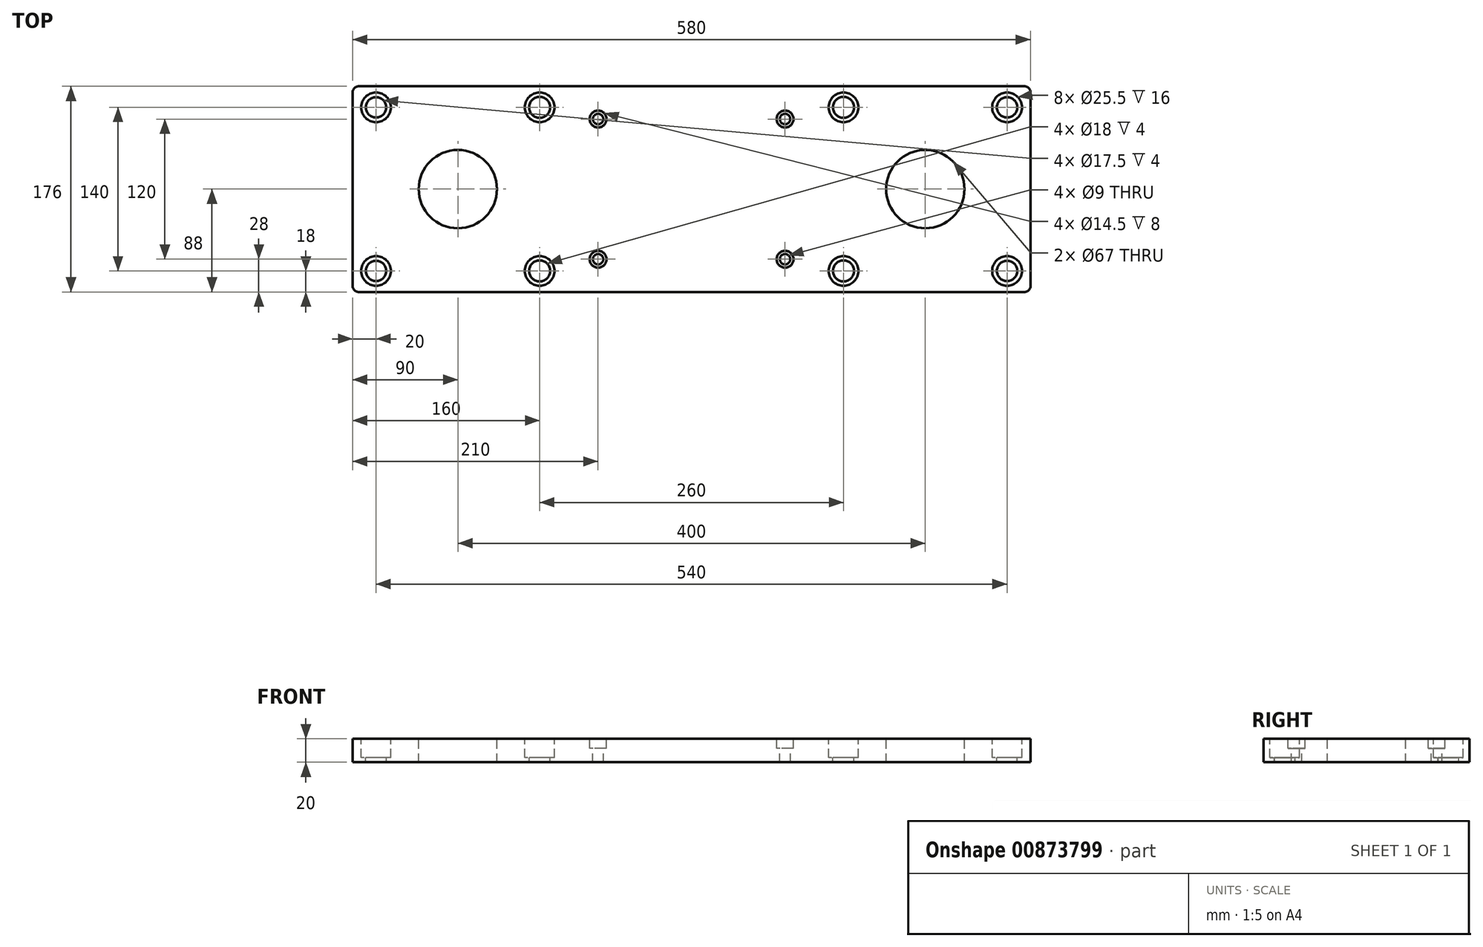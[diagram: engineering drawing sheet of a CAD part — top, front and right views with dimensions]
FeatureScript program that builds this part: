
annotation { "Feature Type Name" : "Feature", "Feature Type Description" : "" }
export const myFeature = defineFeature(function(context is Context, id is Id, definition is map)
    precondition{}
    {
        {
            var Q0;
            Q0=qCreatedBy(makeId("Top.planeOp"),FACE);
            var sketch = newSketch(context, id + "F0", { "sketchPlane" : qUnion([Q0])});
            skLineSegment(sketch, "E0.bottom", {"start": v(290, -88) * mm, "end": v(-290, -88) * mm});
            skLineSegment(sketch, "E0.top", {"start": v(290, 88) * mm, "end": v(-290, 88) * mm});
            skLineSegment(sketch, "E0.left", {"start": v(290, -88) * mm, "end": v(290, 88) * mm});
            skLineSegment(sketch, "E0.right", {"start": v(-290, -88) * mm, "end": v(-290, 88) * mm});
            skPoint(sketch, "E0.middle", {"position": v(0, 0) * mm});
            skLineSegment(sketch, "E1.bottom", {"start": v(-270, -70) * mm, "end": v(-130, -70) * mm});
            skLineSegment(sketch, "E1.top", {"start": v(-270, 70) * mm, "end": v(-130, 70) * mm});
            skLineSegment(sketch, "E1.left", {"start": v(-270, -70) * mm, "end": v(-270, 70) * mm});
            skLineSegment(sketch, "E1.right", {"start": v(-130, -70) * mm, "end": v(-130, 70) * mm, "construction": true});
            skPoint(sketch, "E1.middle", {"position": v(-200, 0) * mm});
            skLineSegment(sketch, "E2.bottom", {"start": v(130, -70) * mm, "end": v(270, -70) * mm});
            skLineSegment(sketch, "E2.top", {"start": v(130, 70) * mm, "end": v(270, 70) * mm});
            skLineSegment(sketch, "E2.left", {"start": v(130, -70) * mm, "end": v(130, 70) * mm, "construction": true});
            skLineSegment(sketch, "E2.right", {"start": v(270, -70) * mm, "end": v(270, 70) * mm});
            skPoint(sketch, "E2.middle", {"position": v(200, 0) * mm});
            skCircle(sketch, "E3", {"center": v(-200, 0) * mm, "radius": 33.5 * mm});
            skCircle(sketch, "E4", {"center": v(200, 0) * mm, "radius": 33.5 * mm});
            skCircle(sketch, "E5", {"center": v(130, 70) * mm, "radius": 9 * mm});
            skCircle(sketch, "E6", {"center": v(130, -70) * mm, "radius": 9 * mm});
            skCircle(sketch, "E7", {"center": v(270, -70) * mm, "radius": 9 * mm});
            skCircle(sketch, "E8", {"center": v(270, 70) * mm, "radius": 9 * mm});
            skCircle(sketch, "E9", {"center": v(-270, 70) * mm, "radius": 9 * mm});
            skCircle(sketch, "E10", {"center": v(-130, 70) * mm, "radius": 9 * mm});
            skCircle(sketch, "E11", {"center": v(-130, -70) * mm, "radius": 9 * mm});
            skCircle(sketch, "E12", {"center": v(-270, -70) * mm, "radius": 9 * mm});
            skLineSegment(sketch, "E13", {"start": v(-200, 0) * mm, "end": v(0, 0) * mm, "construction": true});
            skLineSegment(sketch, "E14", {"start": v(200, 0) * mm, "end": v(0, 0) * mm});
            skCircle(sketch, "E15", {"center": v(0, 0) * mm, "radius": 88.5 * mm, "construction": true});
            skLineSegment(sketch, "E16.bottom", {"start": v(288, 88) * mm, "end": v(112, 88) * mm, "construction": true});
            skLineSegment(sketch, "E16.top", {"start": v(288, -88) * mm, "end": v(112, -88) * mm, "construction": true});
            skLineSegment(sketch, "E16.left", {"start": v(288, 88) * mm, "end": v(288, -88) * mm, "construction": true});
            skLineSegment(sketch, "E16.right", {"start": v(112, 88) * mm, "end": v(112, -88) * mm, "construction": true});
            skLineSegment(sketch, "E17.bottom", {"start": v(-112, 88) * mm, "end": v(-288, 88) * mm, "construction": true});
            skLineSegment(sketch, "E17.top", {"start": v(-112, -88) * mm, "end": v(-288, -88) * mm, "construction": true});
            skLineSegment(sketch, "E17.left", {"start": v(-112, 88) * mm, "end": v(-112, -88) * mm, "construction": true});
            skLineSegment(sketch, "E17.right", {"start": v(-288, 88) * mm, "end": v(-288, -88) * mm, "construction": true});
            skLineSegment(sketch, "E18.bottom", {"start": v(80, 60) * mm, "end": v(-80, 60) * mm});
            skLineSegment(sketch, "E18.top", {"start": v(80, -60) * mm, "end": v(-80, -60) * mm});
            skLineSegment(sketch, "E18.left", {"start": v(80, 60) * mm, "end": v(80, -60) * mm});
            skLineSegment(sketch, "E18.right", {"start": v(-80, 60) * mm, "end": v(-80, -60) * mm});
            skSolve(sketch);
        }
        {
            var Q0;
            Q0=makeQuery(id+"F0.imprint","IMPRINT",FACE,{"disambiguationData":[TD([[makeQuery(id+"F0.imprint","IMPRINT",EDGE,{"derivedFrom":sQuery(id+"F0.wireOp",EDGE,"E0.bottom")}),-1.0]])]});
            var Q1;
            {var subQ0=sQuery(id+"F0.wireOp",EDGE,"E1.right");var subQ1=sQuery(id+"F0.wireOp",EDGE,"E1.top");var subQ2=makeQuery(id+"F0.imprint","INTERSECT",VERTEX,{"derivedFrom":[subQ1,subQ0]});Q1=makeQuery(id+"F0.imprint","IMPRINT",FACE,{"disambiguationData":[TD([[makeQuery(id+"F0.imprint","IMPRINT",EDGE,{"disambiguationData":[TD([[subQ2,1.0]])],"derivedFrom":subQ1}),1.0]])]});}
            var Q2;
            Q2=makeQuery(id+"F0.imprint","IMPRINT",FACE,{"disambiguationData":[TD([[makeQuery(id+"F0.imprint","IMPRINT",EDGE,{"derivedFrom":sQuery(id+"F0.wireOp",EDGE,"E3")}),-1.0]])]});
            var Q3;
            {var subQ0=sQuery(id+"F0.wireOp",EDGE,"E1.left");var subQ1=sQuery(id+"F0.wireOp",EDGE,"E1.top");var subQ2=makeQuery(id+"F0.imprint","INTERSECT",VERTEX,{"derivedFrom":[subQ1,subQ0]});Q3=makeQuery(id+"F0.imprint","IMPRINT",FACE,{"disambiguationData":[TD([[makeQuery(id+"F0.imprint","IMPRINT",EDGE,{"disambiguationData":[TD([[subQ2,-1.0]])],"derivedFrom":subQ1}),1.0]])]});}
            var Q4;
            {var subQ0=sQuery(id+"F0.wireOp",EDGE,"E1.left");var subQ1=sQuery(id+"F0.wireOp",EDGE,"E1.top");var subQ2=makeQuery(id+"F0.imprint","INTERSECT",VERTEX,{"derivedFrom":[subQ1,subQ0]});Q4=makeQuery(id+"F0.imprint","IMPRINT",FACE,{"disambiguationData":[TD([[makeQuery(id+"F0.imprint","IMPRINT",EDGE,{"disambiguationData":[TD([[subQ2,-1.0]])],"derivedFrom":subQ1}),-1.0]])]});}
            var Q5;
            {var subQ0=sQuery(id+"F0.wireOp",EDGE,"E1.right");var subQ1=sQuery(id+"F0.wireOp",EDGE,"E1.top");var subQ2=makeQuery(id+"F0.imprint","INTERSECT",VERTEX,{"derivedFrom":[subQ1,subQ0]});Q5=makeQuery(id+"F0.imprint","IMPRINT",FACE,{"disambiguationData":[TD([[makeQuery(id+"F0.imprint","IMPRINT",EDGE,{"disambiguationData":[TD([[subQ2,1.0]])],"derivedFrom":subQ1}),-1.0]])]});}
            var Q6;
            {var subQ0=sQuery(id+"F0.wireOp",EDGE,"E1.right");var subQ1=sQuery(id+"F0.wireOp",EDGE,"E1.bottom");var subQ2=makeQuery(id+"F0.imprint","INTERSECT",VERTEX,{"derivedFrom":[subQ1,subQ0]});Q6=makeQuery(id+"F0.imprint","IMPRINT",FACE,{"disambiguationData":[TD([[makeQuery(id+"F0.imprint","IMPRINT",EDGE,{"disambiguationData":[TD([[subQ2,1.0]])],"derivedFrom":subQ1}),-1.0]])]});}
            var Q7;
            {var subQ0=sQuery(id+"F0.wireOp",EDGE,"E1.left");var subQ1=sQuery(id+"F0.wireOp",EDGE,"E1.bottom");var subQ2=makeQuery(id+"F0.imprint","INTERSECT",VERTEX,{"derivedFrom":[subQ1,subQ0]});Q7=makeQuery(id+"F0.imprint","IMPRINT",FACE,{"disambiguationData":[TD([[makeQuery(id+"F0.imprint","IMPRINT",EDGE,{"disambiguationData":[TD([[subQ2,-1.0]])],"derivedFrom":subQ1}),1.0]])]});}
            var Q8;
            {var subQ0=sQuery(id+"F0.wireOp",EDGE,"E2.right");var subQ1=sQuery(id+"F0.wireOp",EDGE,"E2.top");var subQ2=makeQuery(id+"F0.imprint","INTERSECT",VERTEX,{"derivedFrom":[subQ1,subQ0]});Q8=makeQuery(id+"F0.imprint","IMPRINT",FACE,{"disambiguationData":[TD([[makeQuery(id+"F0.imprint","IMPRINT",EDGE,{"disambiguationData":[TD([[subQ2,1.0]])],"derivedFrom":subQ1}),-1.0]])]});}
            var Q9;
            {var subQ0=sQuery(id+"F0.wireOp",EDGE,"E2.left");var subQ1=sQuery(id+"F0.wireOp",EDGE,"E2.top");var subQ2=makeQuery(id+"F0.imprint","INTERSECT",VERTEX,{"derivedFrom":[subQ1,subQ0]});Q9=makeQuery(id+"F0.imprint","IMPRINT",FACE,{"disambiguationData":[TD([[makeQuery(id+"F0.imprint","IMPRINT",EDGE,{"disambiguationData":[TD([[subQ2,-1.0]])],"derivedFrom":subQ1}),-1.0]])]});}
            var Q10;
            {var subQ0=sQuery(id+"F0.wireOp",EDGE,"E2.left");var subQ1=sQuery(id+"F0.wireOp",EDGE,"E2.bottom");var subQ2=makeQuery(id+"F0.imprint","INTERSECT",VERTEX,{"derivedFrom":[subQ1,subQ0]});Q10=makeQuery(id+"F0.imprint","IMPRINT",FACE,{"disambiguationData":[TD([[makeQuery(id+"F0.imprint","IMPRINT",EDGE,{"disambiguationData":[TD([[subQ2,-1.0]])],"derivedFrom":subQ1}),-1.0]])]});}
            var Q11;
            {var subQ0=sQuery(id+"F0.wireOp",EDGE,"E2.right");var subQ1=sQuery(id+"F0.wireOp",EDGE,"E2.bottom");var subQ2=makeQuery(id+"F0.imprint","INTERSECT",VERTEX,{"derivedFrom":[subQ1,subQ0]});Q11=makeQuery(id+"F0.imprint","IMPRINT",FACE,{"disambiguationData":[TD([[makeQuery(id+"F0.imprint","IMPRINT",EDGE,{"disambiguationData":[TD([[subQ2,1.0]])],"derivedFrom":subQ1}),1.0]])]});}
            var Q12;
            {var subQ0=sQuery(id+"F0.wireOp",EDGE,"E1.right");var subQ1=sQuery(id+"F0.wireOp",EDGE,"E1.bottom");var subQ2=makeQuery(id+"F0.imprint","INTERSECT",VERTEX,{"derivedFrom":[subQ1,subQ0]});Q12=makeQuery(id+"F0.imprint","IMPRINT",FACE,{"disambiguationData":[TD([[makeQuery(id+"F0.imprint","IMPRINT",EDGE,{"disambiguationData":[TD([[subQ2,1.0]])],"derivedFrom":subQ1}),1.0]])]});}
            var Q13;
            {var subQ0=sQuery(id+"F0.wireOp",EDGE,"E1.left");var subQ1=sQuery(id+"F0.wireOp",EDGE,"E1.bottom");var subQ2=makeQuery(id+"F0.imprint","INTERSECT",VERTEX,{"derivedFrom":[subQ1,subQ0]});Q13=makeQuery(id+"F0.imprint","IMPRINT",FACE,{"disambiguationData":[TD([[makeQuery(id+"F0.imprint","IMPRINT",EDGE,{"disambiguationData":[TD([[subQ2,-1.0]])],"derivedFrom":subQ1}),-1.0]])]});}
            var Q14;
            {var subQ0=sQuery(id+"F0.wireOp",EDGE,"E2.right");var subQ1=sQuery(id+"F0.wireOp",EDGE,"E2.bottom");var subQ2=makeQuery(id+"F0.imprint","INTERSECT",VERTEX,{"derivedFrom":[subQ1,subQ0]});Q14=makeQuery(id+"F0.imprint","IMPRINT",FACE,{"disambiguationData":[TD([[makeQuery(id+"F0.imprint","IMPRINT",EDGE,{"disambiguationData":[TD([[subQ2,1.0]])],"derivedFrom":subQ1}),-1.0]])]});}
            var Q15;
            {var subQ0=sQuery(id+"F0.wireOp",EDGE,"E2.left");var subQ1=sQuery(id+"F0.wireOp",EDGE,"E2.top");var subQ2=makeQuery(id+"F0.imprint","INTERSECT",VERTEX,{"derivedFrom":[subQ1,subQ0]});Q15=makeQuery(id+"F0.imprint","IMPRINT",FACE,{"disambiguationData":[TD([[makeQuery(id+"F0.imprint","IMPRINT",EDGE,{"disambiguationData":[TD([[subQ2,-1.0]])],"derivedFrom":subQ1}),1.0]])]});}
            var Q16;
            {var subQ0=sQuery(id+"F0.wireOp",EDGE,"E2.right");var subQ1=sQuery(id+"F0.wireOp",EDGE,"E2.top");var subQ2=makeQuery(id+"F0.imprint","INTERSECT",VERTEX,{"derivedFrom":[subQ1,subQ0]});Q16=makeQuery(id+"F0.imprint","IMPRINT",FACE,{"disambiguationData":[TD([[makeQuery(id+"F0.imprint","IMPRINT",EDGE,{"disambiguationData":[TD([[subQ2,1.0]])],"derivedFrom":subQ1}),1.0]])]});}
            var Q17;
            {var subQ0=sQuery(id+"F0.wireOp",EDGE,"E2.left");var subQ1=sQuery(id+"F0.wireOp",EDGE,"E2.bottom");var subQ2=makeQuery(id+"F0.imprint","INTERSECT",VERTEX,{"derivedFrom":[subQ1,subQ0]});Q17=makeQuery(id+"F0.imprint","IMPRINT",FACE,{"disambiguationData":[TD([[makeQuery(id+"F0.imprint","IMPRINT",EDGE,{"disambiguationData":[TD([[subQ2,-1.0]])],"derivedFrom":subQ1}),1.0]])]});}
            var Q18;
            Q18=makeQuery(id+"F0.imprint","IMPRINT",FACE,{"disambiguationData":[TD([[makeQuery(id+"F0.imprint","IMPRINT",EDGE,{"derivedFrom":sQuery(id+"F0.wireOp",EDGE,"E4")}),-1.0]])]});
            var Q19;
            Q19=makeQuery(id+"F0.imprint","IMPRINT",FACE,{"disambiguationData":[TD([[makeQuery(id+"F0.imprint","IMPRINT",EDGE,{"derivedFrom":sQuery(id+"F0.wireOp",EDGE,"LPv2xc58-qmmP-0oZ0-BvXn-dd1612CMjPVo")}),-1.0]])]});
            var Q20;
            {var subQ0=sQuery(id+"F0.wireOp",EDGE,"E10");var subQ1=sQuery(id+"F0.wireOp",EDGE,"E0.top");var subQ2=makeQuery(id+"F0.imprint","INTERSECT",VERTEX,{"disambiguationData":[OD(1.0)],"derivedFrom":[subQ1,subQ0]});Q20=makeQuery(id+"F0.imprint","IMPRINT",FACE,{"disambiguationData":[TD([[makeQuery(id+"F0.imprint","IMPRINT",EDGE,{"disambiguationData":[TD([[subQ2,-1.0]])],"derivedFrom":subQ1}),1.0]])]});}
            var Q21;
            {var subQ0=sQuery(id+"F0.wireOp",EDGE,"E8");var subQ1=sQuery(id+"F0.wireOp",EDGE,"E0.top");var subQ2=makeQuery(id+"F0.imprint","INTERSECT",VERTEX,{"disambiguationData":[OD(1.0)],"derivedFrom":[subQ1,subQ0]});Q21=makeQuery(id+"F0.imprint","IMPRINT",FACE,{"disambiguationData":[TD([[makeQuery(id+"F0.imprint","IMPRINT",EDGE,{"disambiguationData":[TD([[subQ2,-1.0]])],"derivedFrom":subQ1}),1.0]])]});}
            var Q22;
            {var subQ5=sQuery(id+"F0.wireOp",EDGE,"E0.left");Q22=makeQuery(id+"F0.imprint","IMPRINT",FACE,{"disambiguationData":[TD([[makeQuery(id+"F0.imprint","IMPRINT",EDGE,{"derivedFrom":subQ5}),1.0]])]});}
            var Q23;
            {var subQ0=sQuery(id+"F0.wireOp",EDGE,"E0.right");Q23=makeQuery(id+"F0.imprint","IMPRINT",FACE,{"disambiguationData":[TD([[makeQuery(id+"F0.imprint","IMPRINT",EDGE,{"derivedFrom":subQ0}),-1.0]])]});}
            var Q24;
            {var subQ3=sQuery(id+"F0.wireOp",EDGE,"E18.bottom");Q24=makeQuery(id+"F0.imprint","IMPRINT",FACE,{"disambiguationData":[TD([[makeQuery(id+"F0.imprint","IMPRINT",EDGE,{"derivedFrom":subQ3}),1.0]])]});}
            extrude(context, id + "F1", {"entities" : qUnion([Q0, Q1, Q2, Q3, Q4, Q5, Q6, Q7, Q8, Q9, Q10, Q11, Q12, Q13, Q14, Q15, Q16, Q17, Q18, Q19, Q20, Q21, Q22, Q23, Q24]), "oppositeDirection" : true, "depth" : 20 * mm, "offsetDistance" : 25 * mm});
        }
        {
            var Q0;
            Q0=sQuery(id+"F0.wireOp",VERTEX,"E1.bottom.start");
            var Q1;
            Q1=sQuery(id+"F0.wireOp",VERTEX,"E1.bottom.end");
            var Q2;
            Q2=sQuery(id+"F0.wireOp",VERTEX,"E1.top.end");
            var Q3;
            Q3=sQuery(id+"F0.wireOp",VERTEX,"E1.top.start");
            var Q4;
            Q4=sQuery(id+"F0.wireOp",VERTEX,"E2.bottom.start");
            var Q5;
            Q5=sQuery(id+"F0.wireOp",VERTEX,"E2.bottom.end");
            var Q6;
            Q6=sQuery(id+"F0.wireOp",VERTEX,"E2.top.end");
            var Q7;
            Q7=sQuery(id+"F0.wireOp",VERTEX,"E2.top.start");
            var Q8;
            Q8=makeQuery(id+"F1.opExtrude","SWEPT_BODY",BODY,{"disambiguationData":[OSD([sQuery(id+"F0.wireOp",EDGE,"E0.bottom"),sQuery(id+"F0.wireOp",EDGE,"E0.top"),sQuery(id+"F0.wireOp",EDGE,"E0.left"),sQuery(id+"F0.wireOp",EDGE,"E0.right"),sQuery(id+"F0.wireOp",EDGE,"E3"),sQuery(id+"F0.wireOp",EDGE,"E4"),sQuery(id+"F0.wireOp",EDGE,"LPv2xc58-qmmP-0oZ0-BvXn-dd1612CMjPVo")])]});
            hole(context, id + "F2", {"style" : HoleStyle.C_BORE, "endStyle" : HoleEndStyle.THROUGH, "standardTappedOrClearance" : lookupTablePath({ "fit" : "Normal", "standard" : "ISO", "size" : "M16", "type" : "Clearance" }), "standardBlindInLast" : lookupTablePath({ "fit" : "Normal", "standard" : "ISO", "engagement" : "75%", "pitch" : "2 mm", "size" : "M16", "type" : "Clearance & tapped" }), "holeDiameter" : 17.5 * mm, "cBoreDiameter" : 25.5 * mm, "cBoreDepth" : 16 * mm, "majorDiameter" : 16 * mm, "isTappedThrough" : true, "tappedDepth" : 12 * mm, "tapClearance" : 3, "locations" : qUnion([Q0, Q1, Q2, Q3, Q4, Q5, Q6, Q7]), "scope" : qUnion([Q8])});
        }
        {
            var Q0;
            Q0=makeQuery(id+"F1.opExtrude","SWEPT_EDGE",EDGE,{"disambiguationData":[OSD([sQuery(id+"F0.wireOp",EDGE,"E0.bottom"),sQuery(id+"F0.wireOp",EDGE,"E0.left")])]});
            var Q1;
            Q1=makeQuery(id+"F1.opExtrude","SWEPT_EDGE",EDGE,{"disambiguationData":[OSD([sQuery(id+"F0.wireOp",EDGE,"E0.top"),sQuery(id+"F0.wireOp",EDGE,"E0.left")])]});
            var Q2;
            Q2=makeQuery(id+"F1.opExtrude","SWEPT_EDGE",EDGE,{"disambiguationData":[OSD([sQuery(id+"F0.wireOp",EDGE,"E0.bottom"),sQuery(id+"F0.wireOp",EDGE,"E0.right")])]});
            var Q3;
            Q3=makeQuery(id+"F1.opExtrude","SWEPT_EDGE",EDGE,{"disambiguationData":[OSD([sQuery(id+"F0.wireOp",EDGE,"E0.top"),sQuery(id+"F0.wireOp",EDGE,"E0.right")])]});
            fillet(context, id + "F3", {"entities" : qUnion([Q0, Q1, Q2, Q3]), "radius" : 5 * mm, "tangentPropagation" : true, "defaultsChanged" : true, "vertexSettings" : [], "allowEdgeOverflow" : false});
        }
        {
            var Q0;
            Q0=sQuery(id+"F0.wireOp",VERTEX,"E18.top.end");
            var Q1;
            Q1=sQuery(id+"F0.wireOp",VERTEX,"E18.top.start");
            var Q2;
            Q2=sQuery(id+"F0.wireOp",VERTEX,"E18.bottom.start");
            var Q3;
            Q3=sQuery(id+"F0.wireOp",VERTEX,"E18.bottom.end");
            var Q4;
            Q4=makeQuery(id+"F1.opExtrude","SWEPT_BODY",BODY,{"disambiguationData":[OSD([sQuery(id+"F0.wireOp",EDGE,"E0.bottom"),sQuery(id+"F0.wireOp",EDGE,"E0.top"),sQuery(id+"F0.wireOp",EDGE,"E0.left"),sQuery(id+"F0.wireOp",EDGE,"E0.right"),sQuery(id+"F0.wireOp",EDGE,"E3"),sQuery(id+"F0.wireOp",EDGE,"E4"),sQuery(id+"F0.wireOp",EDGE,"E5"),sQuery(id+"F0.wireOp",EDGE,"E6"),sQuery(id+"F0.wireOp",EDGE,"E10"),sQuery(id+"F0.wireOp",EDGE,"E11")])]});
            hole(context, id + "F4", {"style" : HoleStyle.C_BORE, "endStyle" : HoleEndStyle.THROUGH, "holeDiameter" : 9 * mm, "cBoreDiameter" : 14.5 * mm, "cBoreDepth" : 8 * mm, "majorDiameter" : 5 * mm, "isTappedThrough" : true, "tappedDepth" : 12 * mm, "tapClearance" : 3, "locations" : qUnion([Q0, Q1, Q2, Q3]), "scope" : qUnion([Q4])});
        }
    });
